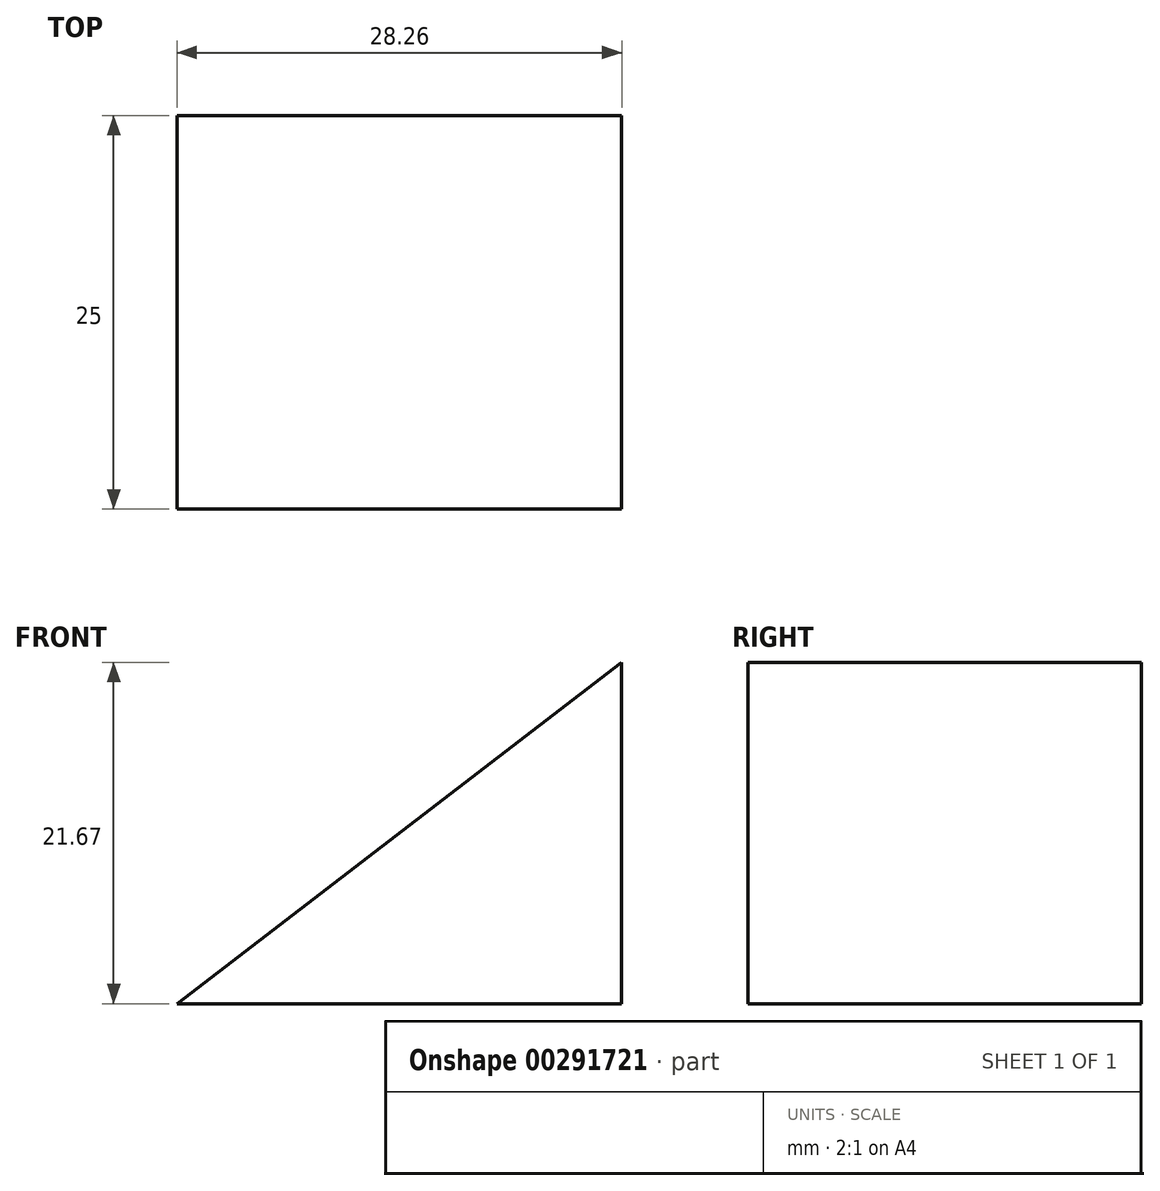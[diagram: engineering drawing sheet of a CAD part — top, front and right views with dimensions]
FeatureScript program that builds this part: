
annotation { "Feature Type Name" : "Feature", "Feature Type Description" : "" }
export const myFeature = defineFeature(function(context is Context, id is Id, definition is map)
    precondition{}
    {
        {
            var Q0;
            Q0=qCreatedBy(makeId("Front.planeOp"),FACE);
            var sketch = newSketch(context, id + "F0", { "sketchPlane" : qUnion([Q0])});
            skLineSegment(sketch, "E0", {"start": v(0, 0) * mm, "end": v(28.26, 21.67) * mm});
            skLineSegment(sketch, "E1", {"start": v(28.26, 0) * mm, "end": v(28.26, 21.67) * mm});
            skLineSegment(sketch, "E2", {"start": v(0, 0) * mm, "end": v(28.26, 0) * mm});
            skSolve(sketch);
        }
        {
            var Q0;
            Q0=makeQuery(id+"F0.imprint","IMPRINT",FACE,{"disambiguationData":[TD([[makeQuery(id+"F0.imprint","IMPRINT",EDGE,{"derivedFrom":sQuery(id+"F0.wireOp",EDGE,"E0")}),-1.0]])]});
            extrude(context, id + "F1", {"entities" : qUnion([Q0]), "endBound" : BoundingType.SYMMETRIC, "depth" : 25 * mm});
        }
    });
